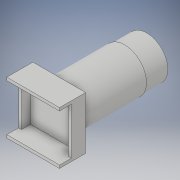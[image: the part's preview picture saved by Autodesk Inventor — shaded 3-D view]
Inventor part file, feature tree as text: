
AUTODESK INVENTOR PART (.ipt)
format: ipt  version: 2018 (Build 220112000, 112)  size: 140,288 bytes
history: native  units: in
note: dims shown in document units (in); Inventor stores cm internally (conversion verified against a paired STEP export)
features: extrude x5, sketch x5
ambient origin geometry x8: Origin, YZ Plane, XZ Plane, XY Plane, X Axis, Y Axis, Z Axis, Center Point
bodies: Solid1 (feature_tree)
feature tree (10):
  extrude  "Extrusion1"  Depth=0.6988in
  extrude  "Extrusion2"  Depth=0.3465in
  extrude  "Extrusion3"  Depth=0.8661in
  extrude  "Extrusion5"  Depth=0.0394in
  extrude  "Extrusion6"  Depth=0.2756in TaperAngle=0.0deg
  sketch  "Sketch1"  dims[d0=0.6988in d1=0.6988in]
  sketch  "Sketch2"  dims[d2=0.3465in d3=0.0in d4=0.5807in]
  sketch  "Sketch3"  dims[d5=0.8661in d6=0.0in d7=0.5556in]
  sketch  "Sketch5"  dims[d8=0.2953in d9=0.0in d14=0.0394in]
  sketch  "Sketch6"  dims[d15=0.0394in d16=0.2756in d17=0.0in d18=0.1575in d19=0.0in]
